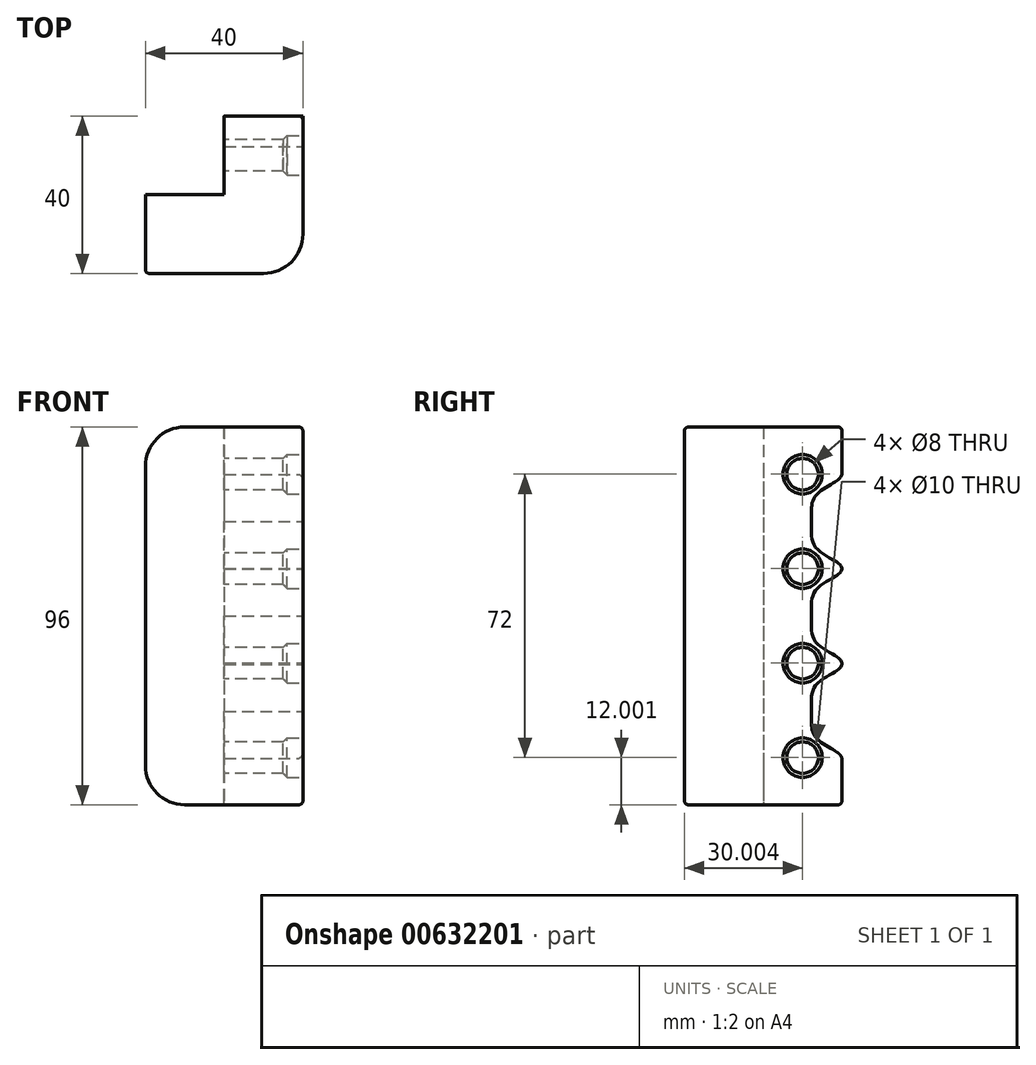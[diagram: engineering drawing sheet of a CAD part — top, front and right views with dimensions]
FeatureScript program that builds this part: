
annotation { "Feature Type Name" : "Feature", "Feature Type Description" : "" }
export const myFeature = defineFeature(function(context is Context, id is Id, definition is map)
    precondition{}
    {
        {
            var Q0;
            Q0=qCreatedBy(makeId("Right.planeOp"),FACE);
            var sketch = newSketch(context, id + "F0", { "sketchPlane" : qUnion([Q0])});
            skCircle(sketch, "E0", {"center": v(-7.59, 36.42) * mm, "radius": 4 * mm});
            skCircle(sketch, "E1.0.1.0", {"center": v(-7.59, 12.42) * mm, "radius": 4 * mm});
            skCircle(sketch, "E1.0.2.0", {"center": v(-7.59, -11.58) * mm, "radius": 4 * mm});
            skCircle(sketch, "E1.0.3.0", {"center": v(-7.59, -35.58) * mm, "radius": 4 * mm});
            skLineSegment(sketch, "E1.direction1", {"start": v(-7.59, 36.42) * mm, "end": v(17.41, 36.42) * mm, "construction": true});
            skLineSegment(sketch, "E1.direction2", {"start": v(-7.59, 36.42) * mm, "end": v(-7.59, 12.42) * mm, "construction": true});
            skLineSegment(sketch, "E2", {"start": v(-37.59, 48.42) * mm, "end": v(-37.59, -47.58) * mm});
            skLineSegment(sketch, "E3", {"start": v(-37.59, -47.58) * mm, "end": v(2.41, -47.58) * mm});
            skLineSegment(sketch, "E4", {"start": v(2.41, -47.58) * mm, "end": v(2.41, 48.42) * mm});
            skLineSegment(sketch, "E5", {"start": v(-37.59, 48.42) * mm, "end": v(2.41, 48.42) * mm});
            skLineSegment(sketch, "E6", {"start": v(-11.59, 36.42) * mm, "end": v(-37.59, 36.42) * mm});
            skSolve(sketch);
        }
        {
            var Q0;
            Q0=makeQuery(id+"F0.imprint","IMPRINT",FACE,{"disambiguationData":[TD([[makeQuery(id+"F0.imprint","IMPRINT",EDGE,{"derivedFrom":sQuery(id+"F0.wireOp",EDGE,"E0")}),-1.0]])]});
            extrude(context, id + "F1", {"entities" : qUnion([Q0]), "depth" : 20 * mm, "offsetDistance" : 25 * mm});
        }
        {
            var Q0;
            Q0=makeQuery(id+"F1.opExtrude","CAP_FACE",FACE,{"disambiguationData":[OSD([sQuery(id+"F0.wireOp",EDGE,"E0"),sQuery(id+"F0.wireOp",EDGE,"E1.0.1.0"),sQuery(id+"F0.wireOp",EDGE,"E1.0.2.0"),sQuery(id+"F0.wireOp",EDGE,"E1.0.3.0"),sQuery(id+"F0.wireOp",EDGE,"E2"),sQuery(id+"F0.wireOp",EDGE,"E3"),sQuery(id+"F0.wireOp",EDGE,"E4"),sQuery(id+"F0.wireOp",EDGE,"E5")])],"isStart":true});
            var sketch = newSketch(context, id + "F2", { "sketchPlane" : qUnion([Q0])});
            skLineSegment(sketch, "E7.bottom", {"start": v(37.59, 48.42) * mm, "end": v(17.59, 48.42) * mm});
            skLineSegment(sketch, "E7.top", {"start": v(37.59, -47.58) * mm, "end": v(17.59, -47.58) * mm});
            skLineSegment(sketch, "E7.left", {"start": v(37.59, 48.42) * mm, "end": v(37.59, -47.58) * mm});
            skLineSegment(sketch, "E7.right", {"start": v(17.59, 48.42) * mm, "end": v(17.59, -47.58) * mm});
            skSolve(sketch);
        }
        {
            var Q0;
            Q0=makeQuery(id+"F2.imprint","IMPRINT",FACE,{"disambiguationData":[TD([[makeQuery(id+"F2.imprint","IMPRINT",EDGE,{"derivedFrom":sQuery(id+"F2.wireOp",EDGE,"E7.bottom")}),1.0]])]});
            extrude(context, id + "F3", {"entities" : qUnion([Q0]), "operationType" : NewBodyOperationType.ADD, "depth" : 20 * mm, "offsetDistance" : 25 * mm});
        }
        {
            var Q0;
            Q0=makeQuery(id+"F1.opExtrude","CAP_FACE",FACE,{"disambiguationData":[OSD([sQuery(id+"F0.wireOp",EDGE,"E0"),sQuery(id+"F0.wireOp",EDGE,"E1.0.1.0"),sQuery(id+"F0.wireOp",EDGE,"E1.0.2.0"),sQuery(id+"F0.wireOp",EDGE,"E1.0.3.0"),sQuery(id+"F0.wireOp",EDGE,"E2"),sQuery(id+"F0.wireOp",EDGE,"E3"),sQuery(id+"F0.wireOp",EDGE,"E4"),sQuery(id+"F0.wireOp",EDGE,"E5")])],"isStart":false});
            var sketch = newSketch(context, id + "F4", { "sketchPlane" : qUnion([Q0])});
            skFitSpline(sketch, "E8", {"points": [v(2.44, 36.42) * mm, v(1.98, 35.55) * mm, v(0.21, 34.19) * mm, v(-4.34, 30.9) * mm, v(-5.38, 27.04) * mm, v(-5.35, 24.42) * mm], "startDerivative": vector(-2.99, -7.52) * mm, "endDerivative": vector(0.4, -12.86) * mm});
            skFitSpline(sketch, "E9.MirrorCS", {"points": [v(2.44, 12.42) * mm, v(1.98, 13.3) * mm, v(0.21, 14.65) * mm, v(-4.34, 17.94) * mm, v(-5.38, 21.8) * mm, v(-5.35, 24.42) * mm], "startDerivative": vector(-2.99, 7.52) * mm, "endDerivative": vector(0.4, 12.86) * mm});
            skFitSpline(sketch, "E10", {"points": [v(2.44, 12.39) * mm, v(1.98, 11.52) * mm, v(0.21, 10.16) * mm, v(-4.34, 6.87) * mm, v(-5.38, 3) * mm, v(-5.35, 0.39) * mm], "startDerivative": vector(-2.99, -7.52) * mm, "endDerivative": vector(0.4, -12.86) * mm});
            skFitSpline(sketch, "E11.MirrorCS", {"points": [v(2.44, -11.61) * mm, v(1.98, -10.74) * mm, v(0.21, -9.38) * mm, v(-4.34, -6.1) * mm, v(-5.38, -2.23) * mm, v(-5.35, 0.39) * mm], "startDerivative": vector(-2.99, 7.52) * mm, "endDerivative": vector(0.4, 12.86) * mm});
            skLineSegment(sketch, "E12", {"start": v(2.44, 12.39) * mm, "end": v(2.44, 12.42) * mm});
            skFitSpline(sketch, "E13", {"points": [v(2.44, -11.8) * mm, v(1.98, -12.68) * mm, v(0.21, -14.04) * mm, v(-4.34, -17.32) * mm, v(-5.38, -21.19) * mm, v(-5.35, -23.8) * mm], "startDerivative": vector(-2.99, -7.52) * mm, "endDerivative": vector(0.4, -12.86) * mm});
            skFitSpline(sketch, "E14.MirrorCS", {"points": [v(2.44, -35.8) * mm, v(1.98, -34.93) * mm, v(0.21, -33.57) * mm, v(-4.34, -30.29) * mm, v(-5.38, -26.42) * mm, v(-5.35, -23.8) * mm], "startDerivative": vector(-2.99, 7.52) * mm, "endDerivative": vector(0.4, 12.86) * mm});
            skLineSegment(sketch, "E15", {"start": v(2.44, -11.61) * mm, "end": v(2.44, -11.8) * mm});
            skLineSegment(sketch, "E16", {"start": v(2.44, -35.8) * mm, "end": v(6.34, -35.8) * mm});
            skLineSegment(sketch, "E17", {"start": v(6.34, -35.8) * mm, "end": v(6.19, 36.42) * mm});
            skLineSegment(sketch, "E18", {"start": v(6.19, 36.42) * mm, "end": v(2.44, 36.42) * mm});
            skSolve(sketch);
        }
        {
            var Q0;
            Q0 = qSketchRegion(id + "F4", true);
            extrude(context, id + "F5", {"entities" : qUnion([Q0]), "operationType" : NewBodyOperationType.REMOVE, "oppositeDirection" : true, "depth" : 20 * mm, "offsetDistance" : 25 * mm});
        }
        {
            var Q0;
            Q0=makeQuery(id+"F3.opExtrude","CAP_EDGE",EDGE,{"disambiguationData":[OSD([sQuery(id+"F2.wireOp",EDGE,"E7.bottom")])],"isStart":false});
            var Q1;
            Q1=makeQuery(id+"F3.opExtrude","CAP_EDGE",EDGE,{"disambiguationData":[OSD([sQuery(id+"F2.wireOp",EDGE,"E7.top")])],"isStart":false});
            var Q2;
            Q2=makeQuery(id+"F1.opExtrude","CAP_EDGE",EDGE,{"disambiguationData":[OSD([sQuery(id+"F0.wireOp",EDGE,"E2")])],"isStart":false});
            fillet(context, id + "F6", {"entities" : qUnion([Q0, Q1, Q2]), "radius" : 10 * mm, "tangentPropagation" : true, "allowEdgeOverflow" : false});
        }
        {
            var Q0;
            Q0=makeQuery(id+"F5.boolean.opBoolean","COPY",EDGE,{"derivedFrom":makeQuery(id+"F5.opExtrude","CAP_EDGE",EDGE,{"disambiguationData":[OSD([sQuery(id+"F4.wireOp",EDGE,"E9.MirrorCS")])],"isStart":true})});
            var Q1;
            Q1=makeQuery(id+"F5.boolean.opBoolean","COPY",EDGE,{"derivedFrom":makeQuery(id+"F5.opExtrude","CAP_EDGE",EDGE,{"disambiguationData":[OSD([sQuery(id+"F4.wireOp",EDGE,"E8")])],"isStart":true})});
            var Q2;
            {var subQ0=sQuery(id+"F0.wireOp",EDGE,"E5");var subQ1=sQuery(id+"F0.wireOp",EDGE,"E4");Q2=makeQuery(id+"F5.boolean.opBoolean","SPLIT",EDGE,{"disambiguationData":[TD([makeQuery(id+"F1.opExtrude","SWEPT_FACE",FACE,{"disambiguationData":[OSD([subQ0])]})])],"derivedFrom":makeQuery(id+"F1.opExtrude","CAP_EDGE",EDGE,{"disambiguationData":[OSD([subQ1])],"isStart":false})});}
            var Q3;
            Q3=makeQuery(id+"F1.opExtrude","CAP_EDGE",EDGE,{"disambiguationData":[OSD([sQuery(id+"F0.wireOp",EDGE,"E5")])],"isStart":false});
            var Q4;
            Q4=makeQuery(id+"F1.opExtrude","SWEPT_EDGE",EDGE,{"disambiguationData":[OSD([sQuery(id+"F0.wireOp",EDGE,"E4"),sQuery(id+"F0.wireOp",EDGE,"E5")])]});
            var Q5;
            Q5=makeQuery(id+"F1.opExtrude","SWEPT_EDGE",EDGE,{"disambiguationData":[OSD([sQuery(id+"F0.wireOp",EDGE,"E3"),sQuery(id+"F0.wireOp",EDGE,"E4")])]});
            var Q6;
            Q6=makeQuery(id+"F1.opExtrude","CAP_EDGE",EDGE,{"disambiguationData":[OSD([sQuery(id+"F0.wireOp",EDGE,"E3")])],"isStart":false});
            var Q7;
            {var subQ0=sQuery(id+"F0.wireOp",EDGE,"E4");var subQ1=sQuery(id+"F0.wireOp",EDGE,"E3");Q7=makeQuery(id+"F5.boolean.opBoolean","SPLIT",EDGE,{"disambiguationData":[TD([makeQuery(id+"F1.opExtrude","SWEPT_FACE",FACE,{"disambiguationData":[OSD([subQ1])]})])],"derivedFrom":makeQuery(id+"F1.opExtrude","CAP_EDGE",EDGE,{"disambiguationData":[OSD([subQ0])],"isStart":false})});}
            var Q8;
            Q8=makeQuery(id+"F5.boolean.opBoolean","COPY",EDGE,{"derivedFrom":makeQuery(id+"F5.opExtrude","CAP_EDGE",EDGE,{"disambiguationData":[OSD([sQuery(id+"F4.wireOp",EDGE,"E14.MirrorCS")])],"isStart":true})});
            var Q9;
            Q9=makeQuery(id+"F5.boolean.opBoolean","COPY",EDGE,{"derivedFrom":makeQuery(id+"F5.opExtrude","CAP_EDGE",EDGE,{"disambiguationData":[OSD([sQuery(id+"F4.wireOp",EDGE,"E13")])],"isStart":true})});
            var Q10;
            Q10=makeQuery(id+"F5.boolean.opBoolean","COPY",EDGE,{"derivedFrom":makeQuery(id+"F5.opExtrude","CAP_EDGE",EDGE,{"disambiguationData":[OSD([sQuery(id+"F4.wireOp",EDGE,"E11.MirrorCS")])],"isStart":true})});
            var Q11;
            Q11=makeQuery(id+"F5.boolean.opBoolean","COPY",EDGE,{"derivedFrom":makeQuery(id+"F5.opExtrude","CAP_EDGE",EDGE,{"disambiguationData":[OSD([sQuery(id+"F4.wireOp",EDGE,"E10")])],"isStart":true})});
            var Q12;
            Q12=makeQuery(id+"F3.boolean.opBoolean","MERGE",EDGE,{"derivedFrom":[makeQuery(id+"F1.opExtrude","SWEPT_EDGE",EDGE,{"disambiguationData":[OSD([sQuery(id+"F0.wireOp",EDGE,"E2"),sQuery(id+"F0.wireOp",EDGE,"E5")])]}),makeQuery(id+"F3.opExtrude","SWEPT_EDGE",EDGE,{"disambiguationData":[OSD([sQuery(id+"F2.wireOp",EDGE,"E7.bottom"),sQuery(id+"F2.wireOp",EDGE,"E7.left")])]})]});
            fillet(context, id + "F7", {"entities" : qUnion([Q0, Q1, Q2, Q3, Q4, Q5, Q6, Q7, Q8, Q9, Q10, Q11, Q12]), "radius" : 1 * mm, "tangentPropagation" : true, "allowEdgeOverflow" : false});
        }
        {
            var Q0;
            Q0=makeQuery(id+"F1.opExtrude","CAP_FACE",FACE,{"disambiguationData":[OSD([sQuery(id+"F0.wireOp",EDGE,"E0"),sQuery(id+"F0.wireOp",EDGE,"E1.0.1.0"),sQuery(id+"F0.wireOp",EDGE,"E1.0.2.0"),sQuery(id+"F0.wireOp",EDGE,"E1.0.3.0"),sQuery(id+"F0.wireOp",EDGE,"E2"),sQuery(id+"F0.wireOp",EDGE,"E3"),sQuery(id+"F0.wireOp",EDGE,"E4"),sQuery(id+"F0.wireOp",EDGE,"E5")])],"isStart":false});
            var sketch = newSketch(context, id + "F8", { "sketchPlane" : qUnion([Q0])});
            skCircle(sketch, "E19", {"center": v(-7.59, 36.42) * mm, "radius": 5 * mm});
            skCircle(sketch, "E20.0.1.0", {"center": v(-7.59, 12.42) * mm, "radius": 5 * mm});
            skCircle(sketch, "E20.0.2.0", {"center": v(-7.59, -11.58) * mm, "radius": 5 * mm});
            skCircle(sketch, "E20.0.3.0", {"center": v(-7.59, -35.58) * mm, "radius": 5 * mm});
            skLineSegment(sketch, "E20.direction1", {"start": v(-7.59, 36.42) * mm, "end": v(17.41, 36.42) * mm, "construction": true});
            skLineSegment(sketch, "E20.direction2", {"start": v(-7.59, 36.42) * mm, "end": v(-7.59, 12.42) * mm, "construction": true});
            skSolve(sketch);
        }
        {
            var Q0;
            Q0 = qSketchRegion(id + "F8", true);
            extrude(context, id + "F9", {"entities" : qUnion([Q0]), "operationType" : NewBodyOperationType.REMOVE, "oppositeDirection" : true, "depth" : 4 * mm, "offsetDistance" : 25 * mm});
        }
        {
            var Q0;
            Q0=makeQuery(id+"F9.boolean.opBoolean","INTERSECT",EDGE,{"derivedFrom":[makeQuery(id+"F1.opExtrude","SWEPT_FACE",FACE,{"disambiguationData":[OSD([sQuery(id+"F0.wireOp",EDGE,"E0")])]}),makeQuery(id+"F9.opExtrude","CAP_FACE",FACE,{"disambiguationData":[OSD([sQuery(id+"F8.wireOp",EDGE,"E19")])],"isStart":false})]});
            var Q1;
            Q1=makeQuery(id+"F9.boolean.opBoolean","INTERSECT",EDGE,{"derivedFrom":[makeQuery(id+"F1.opExtrude","SWEPT_FACE",FACE,{"disambiguationData":[OSD([sQuery(id+"F0.wireOp",EDGE,"E1.0.1.0")])]}),makeQuery(id+"F9.opExtrude","CAP_FACE",FACE,{"disambiguationData":[OSD([sQuery(id+"F8.wireOp",EDGE,"E20.0.1.0")])],"isStart":false})]});
            var Q2;
            Q2=makeQuery(id+"F9.boolean.opBoolean","INTERSECT",EDGE,{"derivedFrom":[makeQuery(id+"F1.opExtrude","SWEPT_FACE",FACE,{"disambiguationData":[OSD([sQuery(id+"F0.wireOp",EDGE,"E1.0.3.0")])]}),makeQuery(id+"F9.opExtrude","CAP_FACE",FACE,{"disambiguationData":[OSD([sQuery(id+"F8.wireOp",EDGE,"E20.0.3.0")])],"isStart":false})]});
            var Q3;
            Q3=makeQuery(id+"F9.boolean.opBoolean","INTERSECT",EDGE,{"derivedFrom":[makeQuery(id+"F1.opExtrude","SWEPT_FACE",FACE,{"disambiguationData":[OSD([sQuery(id+"F0.wireOp",EDGE,"E1.0.2.0")])]}),makeQuery(id+"F9.opExtrude","CAP_FACE",FACE,{"disambiguationData":[OSD([sQuery(id+"F8.wireOp",EDGE,"E20.0.2.0")])],"isStart":false})]});
            chamfer(context, id + "F10", {"entities" : qUnion([Q0, Q1, Q2, Q3]), "width" : 1 * mm, "tangentPropagation" : true});
        }
    });
